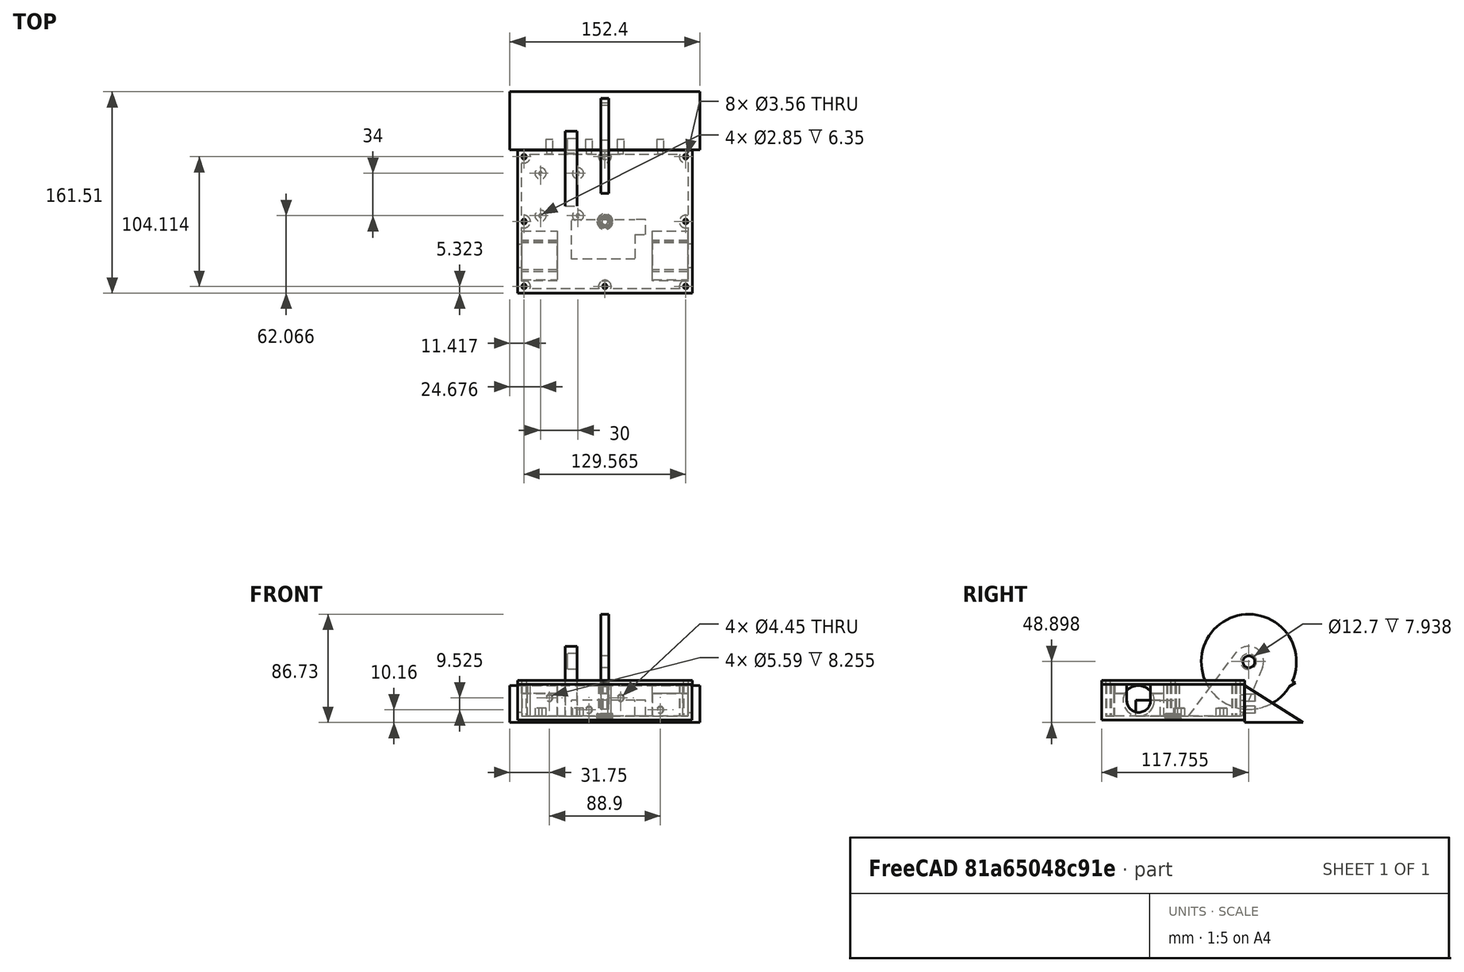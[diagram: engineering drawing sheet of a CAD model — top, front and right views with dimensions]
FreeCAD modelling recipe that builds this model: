
FCSTD DOCUMENT  (FreeCAD 0.20R)
Label: Isaac_combat_robot
License: All rights reserved
LicenseURL: http://en.wikipedia.org/wiki/All_rights_reserved
objects: Sketcher::SketchObject×22, PartDesign::Pad×14, PartDesign::Pocket×7, PartDesign::Body×7, Mesh::Feature×2, Spreadsheet::Sheet×1, PartDesign::ShapeBinder×1, PartDesign::Plane×1, PartDesign::FeatureBase×1, App::DocumentObjectGroup×1, Part::Feature×1
note: 75 computed .brp shape members not serialized (recipe doc carries the construction recipe); baked Part::Feature solids carry a one-line shape summary decoded from their .brp

FEATURE [Sketcher::SketchObject] Sketch
  FullyConstrained = true
  MapMode = 5
  Support = -> [XY_Plane]
  expr: Constraints[20] = Spreadsheet.wall_thickness
  expr: Constraints[21] = Spreadsheet.wall_thickness
  sketch-geometry (8):
    g0: LineSegment StartX=-69.85 StartY=57.15 StartZ=0 EndX=69.85 EndY=57.15 EndZ=0
    g1: LineSegment StartX=69.85 StartY=57.15 StartZ=0 EndX=69.85 EndY=-57.15 EndZ=0
    g2: LineSegment StartX=69.85 StartY=-57.15 StartZ=0 EndX=-69.85 EndY=-57.15 EndZ=0
    g3: LineSegment StartX=-69.85 StartY=-57.15 StartZ=0 EndX=-69.85 EndY=57.15 EndZ=0
    g4: LineSegment StartX=-66.675 StartY=53.975 StartZ=0 EndX=66.675 EndY=53.975 EndZ=0
    g5: LineSegment StartX=66.675 StartY=53.975 StartZ=0 EndX=66.675 EndY=-53.975 EndZ=0
    g6: LineSegment StartX=66.675 StartY=-53.975 StartZ=0 EndX=-66.675 EndY=-53.975 EndZ=0
    g7: LineSegment StartX=-66.675 StartY=-53.975 StartZ=0 EndX=-66.675 EndY=53.975 EndZ=0
  constraints (22):
    c: Coincident(g0,g1)
    c: Coincident(g1,g2)
    c: Coincident(g2,g3)
    c: Coincident(g3,g0)
    c: Horizontal(g0)
    c: Horizontal(g2)
    c: Vertical(g1)
    c: Vertical(g3)
    c: Symmetric(g1,g0,g-1)
    c: DistanceX(g0,g0) = 139.7
    c: DistanceY(g1,g1) = 114.3
    c: Coincident(g4,g5)
    c: Coincident(g5,g6)
    c: Coincident(g6,g7)
    c: Coincident(g7,g4)
    c: Horizontal(g4)
    c: Horizontal(g6)
    c: Vertical(g5)
    c: Vertical(g7)
    c: Symmetric(g5,g4,g-1)
    c: DistanceX(g4,g0) = 3.175
    c: DistanceY(g1,g5) = 3.175
FEATURE [Spreadsheet::Sheet] Spreadsheet
  cells = A1=wall thickness; B1(wall_thickness)==0.125 * 25.4; A2=height; B2(height)==1 * 25.4; A3=base_thickness; B3(base_thickness)==0.125 * 25.4
FEATURE [PartDesign::Pad] Pad  label="walls"
  Direction = (0,0,1)
  Length = 25.4
  Length2 = 100.013
  Profile = -> Sketch
  Type = 0
  expr: Length = Spreadsheet.height
FEATURE [Sketcher::SketchObject] Sketch001
  ExternalGeometry = -> [Pad]
  FullyConstrained = true
  MapMode = 5
  Placement = pos=(0,0,0) rot=(1,0,0;3.14159rad)
  Support = -> [Pad]
  sketch-geometry (4):
    g0: LineSegment StartX=69.85 StartY=57.15 StartZ=0 EndX=-69.85 EndY=57.15 EndZ=0
    g1: LineSegment StartX=-69.85 StartY=57.15 StartZ=0 EndX=-69.85 EndY=-57.15 EndZ=0
    g2: LineSegment StartX=-69.85 StartY=-57.15 StartZ=0 EndX=69.85 EndY=-57.15 EndZ=0
    g3: LineSegment StartX=69.85 StartY=-57.15 StartZ=0 EndX=69.85 EndY=57.15 EndZ=0
  constraints (10):
    c: Coincident(g0,g1)
    c: Coincident(g1,g2)
    c: Coincident(g2,g3)
    c: Coincident(g3,g0)
    c: Horizontal(g0)
    c: Horizontal(g2)
    c: Vertical(g1)
    c: Vertical(g3)
    c: Coincident(g0,g-3)
    c: Coincident(g1,g-4)
FEATURE [PartDesign::Pad] Pad001  label="base"
  BaseFeature = -> Pad
  Direction = (0,0,-1)
  Length = 3.175
  Length2 = 100.013
  Profile = -> Sketch001
  Type = 0
  expr: Length = Spreadsheet.base_thickness
FEATURE [Sketcher::SketchObject] Sketch002
  ExternalGeometry = -> [Pad001]
  FullyConstrained = true
  MapMode = 5
  Support = -> [Pad001]
  sketch-geometry (24):
    g0: LineSegment StartX=-64.77 StartY=52.07 StartZ=0 EndX=64.77 EndY=52.07 EndZ=0
    g1: LineSegment StartX=64.77 StartY=52.07 StartZ=0 EndX=64.77 EndY=-52.07 EndZ=0
    g2: LineSegment StartX=64.77 StartY=-52.07 StartZ=0 EndX=-64.77 EndY=-52.07 EndZ=0
    g3: LineSegment StartX=-64.77 StartY=-52.07 StartZ=0 EndX=-64.77 EndY=52.07 EndZ=0
    g4: GeomPoint X=-64.77 Y=0 Z=0
    g5: GeomPoint X=0 Y=52.07 Z=0
    g6: GeomPoint X=0 Y=-52.07 Z=0
    g7: GeomPoint X=64.77 Y=0 Z=0
    g8: Circle CenterX=-64.77 CenterY=52.07 CenterZ=0 NormalX=0 NormalY=0 NormalZ=1 AngleXU=0 Radius=5.08
    g9: Circle CenterX=0 CenterY=52.07 CenterZ=0 NormalX=0 NormalY=0 NormalZ=1 AngleXU=0 Radius=5.08
    g10: Circle CenterX=64.77 CenterY=52.07 CenterZ=0 NormalX=0 NormalY=0 NormalZ=1 AngleXU=0 Radius=5.08
    g11: Circle CenterX=64.77 CenterY=0 CenterZ=0 NormalX=0 NormalY=0 NormalZ=1 AngleXU=0 Radius=5.08
    g12: Circle CenterX=64.77 CenterY=-52.07 CenterZ=0 NormalX=0 NormalY=0 NormalZ=1 AngleXU=0 Radius=5.08
    g13: Circle CenterX=0 CenterY=-52.07 CenterZ=0 NormalX=0 NormalY=0 NormalZ=1 AngleXU=0 Radius=5.08
    g14: Circle CenterX=-64.77 CenterY=-52.07 CenterZ=0 NormalX=0 NormalY=0 NormalZ=1 AngleXU=0 Radius=5.08
    g15: Circle CenterX=-64.77 CenterY=0 CenterZ=0 NormalX=0 NormalY=0 NormalZ=1 AngleXU=0 Radius=5.08
    g16: Circle CenterX=-64.77 CenterY=52.07 CenterZ=0 NormalX=0 NormalY=0 NormalZ=1 AngleXU=0 Radius=2.413
    g17: Circle CenterX=0 CenterY=52.07 CenterZ=0 NormalX=0 NormalY=0 NormalZ=1 AngleXU=0 Radius=2.413
    g18: Circle CenterX=64.77 CenterY=52.07 CenterZ=0 NormalX=0 NormalY=0 NormalZ=1 AngleXU=0 Radius=2.413
    g19: Circle CenterX=64.77 CenterY=0 CenterZ=0 NormalX=0 NormalY=0 NormalZ=1 AngleXU=0 Radius=2.413
    g20: Circle CenterX=-64.77 CenterY=0 CenterZ=0 NormalX=0 NormalY=0 NormalZ=1 AngleXU=0 Radius=2.413
    g21: Circle CenterX=-64.77 CenterY=-52.07 CenterZ=0 NormalX=0 NormalY=0 NormalZ=1 AngleXU=0 Radius=2.413
    g22: Circle CenterX=0 CenterY=-52.07 CenterZ=0 NormalX=0 NormalY=0 NormalZ=1 AngleXU=0 Radius=2.413
    g23: Circle CenterX=64.77 CenterY=-52.07 CenterZ=0 NormalX=0 NormalY=0 NormalZ=1 AngleXU=0 Radius=2.413
  constraints (51):
    c: Coincident(g0,g1)
    c: Coincident(g1,g2)
    c: Coincident(g2,g3)
    c: Coincident(g3,g0)
    c: Horizontal(g0)
    c: Horizontal(g2)
    c: Vertical(g1)
    c: Vertical(g3)
    c: Symmetric(g1,g0,g-1)
    c: PointOnObject(g4,g3)
    c: PointOnObject(g5,g0)
    c: PointOnObject(g6,g2)
    c: PointOnObject(g7,g1)
    c: PointOnObject(g4,g-1)
    c: PointOnObject(g5,g-2)
    c: PointOnObject(g7,g-1)
    c: PointOnObject(g6,g-2)
    c: Coincident(g8,g0)
    c: Coincident(g9,g5)
    c: Coincident(g10,g0)
    c: Coincident(g11,g7)
    c: Coincident(g12,g1)
    c: Coincident(g13,g6)
    c: Coincident(g14,g2)
    c: Coincident(g15,g4)
    c: Equal(g14,g13)
    c: Equal(g13,g12)
    c: Equal(g12,g11)
    c: Equal(g11,g10)
    c: Equal(g10,g9)
    c: Equal(g9,g8)
    c: Equal(g8,g15)
    c: Diameter(g8) = 10.16
    c: Coincident(g16,g8)
    c: Coincident(g17,g9)
    c: Coincident(g18,g10)
    c: Coincident(g19,g11)
    c: Coincident(g20,g15)
    c: Coincident(g21,g14)
    c: Coincident(g22,g13)
    c: Coincident(g23,g12)
    c: Equal(g23,g22)
    c: Equal(g22,g21)
    c: Equal(g21,g20)
    c: Equal(g20,g16)
    c: Equal(g16,g17)
    c: Equal(g17,g18)
    c: Equal(g18,g19)
    c: Diameter(g18) = 4.826
    c: Tangent(g10,g-4)
    c: Tangent(g10,g-3)
FEATURE [PartDesign::Pad] Pad002  label="brass_insert_holes"
  BaseFeature = -> Pad001
  Direction = (0,0,1)
  Length = 25.4
  Length2 = 100.013
  Profile = -> Sketch002
  Type = 0
  expr: Length = Spreadsheet.height
FEATURE [Sketcher::SketchObject] Sketch003
  ExternalGeometry = -> [Pad002]
  FullyConstrained = true
  MapMode = 5
  Support = -> [Pad002]
  sketch-geometry (8):
    g0: LineSegment StartX=-69.85 StartY=-7.62 StartZ=0 EndX=-38.1 EndY=-7.62 EndZ=0
    g1: LineSegment StartX=-38.1 StartY=-7.62 StartZ=0 EndX=-38.1 EndY=-47.62 EndZ=0
    g2: LineSegment StartX=-38.1 StartY=-47.62 StartZ=0 EndX=-69.85 EndY=-47.62 EndZ=0
    g3: LineSegment StartX=-69.85 StartY=-47.62 StartZ=0 EndX=-69.85 EndY=-7.62 EndZ=0
    g4: LineSegment StartX=38.1 StartY=-7.62 StartZ=0 EndX=69.85 EndY=-7.62 EndZ=0
    g5: LineSegment StartX=69.85 StartY=-7.62 StartZ=0 EndX=69.85 EndY=-47.62 EndZ=0
    g6: LineSegment StartX=69.85 StartY=-47.62 StartZ=0 EndX=38.1 EndY=-47.62 EndZ=0
    g7: LineSegment StartX=38.1 StartY=-47.62 StartZ=0 EndX=38.1 EndY=-7.62 EndZ=0
  constraints (23):
    c: Coincident(g0,g1)
    c: Coincident(g1,g2)
    c: Coincident(g2,g3)
    c: Coincident(g3,g0)
    c: Horizontal(g0)
    c: Horizontal(g2)
    c: Vertical(g1)
    c: Vertical(g3)
    c: PointOnObject(g0,g-3)
    c: Coincident(g4,g5)
    c: Coincident(g5,g6)
    c: Coincident(g6,g7)
    c: Coincident(g7,g4)
    c: Horizontal(g4)
    c: Horizontal(g6)
    c: Vertical(g5)
    c: Vertical(g7)
    c: Equal(g4,g0)
    c: Equal(g1,g7)
    c: Symmetric(g0,g4,g-2)
    c: DistanceX(g0,g0) = 31.75
    c: DistanceY(g7,g7) = 40
    c: DistanceY(g0,g-1) = 7.62
FEATURE [PartDesign::Pad] Pad003  label="motor_pad"
  BaseFeature = -> Pad002
  Direction = (0,0,1)
  Length = 24.5
  Length2 = 99.9998
  Profile = -> Sketch003
  Type = 0
  expr: Length = 24.5mm
FEATURE [Sketcher::SketchObject] Sketch004
  ExternalGeometry = -> [Pad003]
  FullyConstrained = false
  MapMode = 5
  Placement = pos=(-69.85,0,0) rot=(0.57735,-0.57735,-0.57735;2.0944rad)
  Support = -> [Pad003]
  sketch-geometry (5):
    g0: LineSegment StartX=27.62 StartY=36.8625 StartZ=0 EndX=27.62 EndY=-14.5238 EndZ=0
    g1: ArcOfCircle CenterX=27.62 CenterY=12.4993 CenterZ=0 NormalX=0 NormalY=0 NormalZ=1 AngleXU=0 Radius=12.4993 StartAngle=2.43725 EndAngle=6.98752
    g2: LineSegment StartX=18.095 StartY=20.593 StartZ=0 EndX=18.095 EndY=26.943 EndZ=0
    g3: LineSegment StartX=18.095 StartY=26.943 StartZ=0 EndX=37.145 EndY=26.943 EndZ=0
    g4: LineSegment StartX=37.145 StartY=26.943 StartZ=0 EndX=37.145 EndY=20.593 EndZ=0
  constraints (14):
    c: Symmetric(g-4,g-3,g0)
    c: PointOnObject(g1,g0)
    c: Diameter(g1) = 24.9987
    c: Tangent(g1,g-1)
    c: Vertical(g2)
    c: Coincident(g3,g2)
    c: Coincident(g4,g3)
    c: Vertical(g4)
    c: Symmetric(g3,g2,g0)
    c: DistanceX(g3,g3) = 19.05
    c: Coincident(g1,g2)
    c: Coincident(g1,g4)
    c: DistanceY(g4,g4) = 6.35
    c: DistanceX(g-1,g0) = 27.62
FEATURE [PartDesign::Pocket] Pocket  label="drive_motor_pocket"
  BaseFeature = -> Pad003
  Direction = (1,0,0)
  Length = 5.0038
  Length2 = 99.9998
  Profile = -> Sketch004
  Type = 1
FEATURE [Sketcher::SketchObject] Sketch005  label="battery"
  FullyConstrained = false
  sketch-geometry (7):
    g0: LineSegment StartX=-55.3377 StartY=49.4576 StartZ=0 EndX=-23.5877 EndY=49.4576 EndZ=0
    g1: LineSegment StartX=-23.5877 StartY=49.4576 StartZ=0 EndX=-23.5877 EndY=-1.34242 EndZ=0
    g2: LineSegment StartX=-35.7299 StartY=-1.34242 StartZ=0 EndX=-55.3377 EndY=-1.34242 EndZ=0
    g3: LineSegment StartX=-55.3377 StartY=-1.34242 StartZ=0 EndX=-55.3377 EndY=49.4576 EndZ=0
    g4: LineSegment StartX=-35.7299 StartY=-1.34242 StartZ=0 EndX=-35.7299 EndY=-9.80609 EndZ=0
    g5: LineSegment StartX=-35.7299 StartY=-9.80609 StartZ=0 EndX=-23.5877 EndY=-9.80609 EndZ=0
    g6: LineSegment StartX=-23.5877 StartY=-9.80609 StartZ=0 EndX=-23.5877 EndY=-1.34242 EndZ=0
  constraints (14):
    c: Coincident(g0,g1)
    c: Coincident(g2,g3)
    c: Coincident(g3,g0)
    c: Horizontal(g0)
    c: Horizontal(g2)
    c: Vertical(g1)
    c: Vertical(g3)
    c: DistanceX(g0,g0) = 31.75
    c: DistanceY(g1,g1) = 50.8
    c: Coincident(g4,g5)
    c: Coincident(g5,g6)
    c: Horizontal(g5)
    c: Vertical(g4)
    c: Vertical(g6)
FEATURE [Sketcher::SketchObject] Sketch007  label="receiver_footprint"
  AttachmentOffset = pos=(-34.29,25.4,0) rot=(0,0,1;0rad)
  FullyConstrained = false
  MapMode = 5
  Placement = pos=(-34.29,25.4,0) rot=(0,0,1;0rad)
  sketch-geometry (12):
    g0: LineSegment StartX=-17.2344 StartY=13.2858 StartZ=0 EndX=12.7656 EndY=13.2858 EndZ=0
    g1: LineSegment StartX=12.7656 StartY=13.2858 StartZ=0 EndX=12.7656 EndY=-20.7142 EndZ=0
    g2: LineSegment StartX=12.7656 StartY=-20.7142 StartZ=0 EndX=-17.2344 EndY=-20.7142 EndZ=0
    g3: LineSegment StartX=-17.2344 StartY=-20.7142 StartZ=0 EndX=-17.2344 EndY=13.2858 EndZ=0
    g4: Circle CenterX=-17.2344 CenterY=13.2858 CenterZ=0 NormalX=0 NormalY=0 NormalZ=1 AngleXU=0 Radius=1.425
    g5: Circle CenterX=12.7656 CenterY=13.2858 CenterZ=0 NormalX=0 NormalY=0 NormalZ=1 AngleXU=0 Radius=1.425
    g6: Circle CenterX=12.7656 CenterY=-20.7142 CenterZ=0 NormalX=0 NormalY=0 NormalZ=1 AngleXU=0 Radius=1.425
    g7: Circle CenterX=-17.2344 CenterY=-20.7142 CenterZ=0 NormalX=0 NormalY=0 NormalZ=1 AngleXU=0 Radius=1.425
    g8: Circle CenterX=12.7656 CenterY=13.2858 CenterZ=0 NormalX=0 NormalY=0 NormalZ=1 AngleXU=0 Radius=4.445
    g9: Circle CenterX=-17.2344 CenterY=13.2858 CenterZ=0 NormalX=0 NormalY=0 NormalZ=1 AngleXU=0 Radius=4.445
    g10: Circle CenterX=-17.2344 CenterY=-20.7142 CenterZ=0 NormalX=0 NormalY=0 NormalZ=1 AngleXU=0 Radius=4.445
    g11: Circle CenterX=12.7656 CenterY=-20.7142 CenterZ=0 NormalX=0 NormalY=0 NormalZ=1 AngleXU=0 Radius=4.445
  constraints (26):
    c: Coincident(g0,g1)
    c: Coincident(g1,g2)
    c: Coincident(g2,g3)
    c: Coincident(g3,g0)
    c: Horizontal(g0)
    c: Horizontal(g2)
    c: Vertical(g1)
    c: Vertical(g3)
    c: Coincident(g4,g0)
    c: Coincident(g5,g0)
    c: Coincident(g6,g1)
    c: Coincident(g7,g2)
    c: Equal(g7,g6)
    c: Equal(g6,g5)
    c: Equal(g5,g4)
    c: Diameter(g5) = 2.85
    c: DistanceX(g0,g0) = 30
    c: DistanceY(g1,g1) = 34
    c: Coincident(g8,g5)
    c: Coincident(g9,g4)
    c: Coincident(g10,g7)
    c: Coincident(g11,g6)
    c: Equal(g10,g11)
    c: Equal(g11,g8)
    c: Equal(g8,g9)
    c: Diameter(g9) = 8.89
FEATURE [PartDesign::Pad] Pad006  label="receiver-pads"
  BaseFeature = -> Pocket
  Direction = (0,0,1)
  Length = 6.35
  Length2 = 99.9998
  Profile = -> Sketch007
  Type = 0
FEATURE [PartDesign::Pad] Pad007
  Direction = (1,1,1)
  Length = 12.7
  Length2 = 99.9998
  Profile = -> Sketch005
  Type = 0
FEATURE [PartDesign::Body] Body002  label="battery001"
  Group = -> [Sketch005,Pad007]
  Origin = -> Origin002
  Placement = pos=(22.86,25.4,0) rot=(0,0,1;1.5708rad)
  Tip = -> Pad007
FEATURE [PartDesign::ShapeBinder] ReferencePad006
  Support = -> [Pad006]
  TraceSupport = false
FEATURE [Sketcher::SketchObject] Sketch009  label="cover_plate"
  FullyConstrained = false
  MapMode = 5
  Placement = pos=(0,0,25.4) rot=(0,0,1;0rad)
  Support = -> [ReferencePad006]
  sketch-geometry (4):
    g0: LineSegment StartX=-70.0059 StartY=57.1862 StartZ=0 EndX=70.0536 EndY=57.1862 EndZ=0
    g1: LineSegment StartX=70.0536 StartY=57.1862 StartZ=0 EndX=70.0536 EndY=-57.385 EndZ=0
    g2: LineSegment StartX=70.0536 StartY=-57.385 StartZ=0 EndX=-70.0059 EndY=-57.385 EndZ=0
    g3: LineSegment StartX=-70.0059 StartY=-57.385 StartZ=0 EndX=-70.0059 EndY=57.1862 EndZ=0
  constraints (8):
    c: Coincident(g0,g1)
    c: Coincident(g1,g2)
    c: Coincident(g2,g3)
    c: Coincident(g3,g0)
    c: Horizontal(g0)
    c: Horizontal(g2)
    c: Vertical(g1)
    c: Vertical(g3)
FEATURE [PartDesign::Pad] Pad008
  Direction = (0,0,1)
  Length = 3.175
  Length2 = 99.9998
  Profile = -> Sketch009
  Type = 0
FEATURE [Mesh::Feature] body_half  label="switch_body_half"
  Placement = pos=(31.985,-47.375,0) rot=(1,0,0;1.5708rad)
FEATURE [Mesh::Feature] body_half001  label="switch_body_half001"
  Placement = pos=(44.985,-54.375,0) rot=(0,0.707107,0.707107;3.14159rad)
FEATURE [Sketcher::SketchObject] Sketch011
  FullyConstrained = false
  MapMode = 5
  Placement = pos=(0,0,0) rot=(0.57735,0.57735,0.57735;2.0944rad)
  Support = -> [YZ_Plane004]
  sketch-geometry (3):
    g0: LineSegment StartX=57.4696 StartY=-5.08 StartZ=0 EndX=104.128 EndY=-5.08 EndZ=0
    g1: LineSegment StartX=104.128 StartY=-5.08 StartZ=0 EndX=57.4696 EndY=24.511 EndZ=0
    g2: LineSegment StartX=57.4696 StartY=24.511 StartZ=0 EndX=57.4696 EndY=-5.08 EndZ=0
  constraints (7):
    c: Coincident(g0,g1)
    c: Coincident(g1,g2)
    c: Coincident(g2,g0)
    c: Vertical(g2)
    c: Horizontal(g0)
    c: DistanceY(g2,g2) = 29.591
    c: DistanceY(g0,g-1) = 5.08
FEATURE [PartDesign::Pad] Pad009  label="wedge-shape"
  Direction = (1,1,1)
  Length = 152.4
  Length2 = 99.9998
  Midplane = true
  Placement = pos=(0,0,0) rot=(0.57735,0.57735,0.57735;2.0944rad)
  Profile = -> Sketch011
  Type = 0
FEATURE [Sketcher::SketchObject] Sketch013  label="cover-holes"
  FullyConstrained = false
  MapMode = 5
  Placement = pos=(0,0,28.575) rot=(0,0,1;0rad)
  Support = -> [Pad008]
  sketch-geometry (16):
    g0: LineSegment StartX=-70.1798 StartY=57.1112 StartZ=0 EndX=70.1798 EndY=57.1112 EndZ=0
    g1: LineSegment StartX=70.1798 StartY=57.1112 StartZ=0 EndX=70.1798 EndY=-57.1112 EndZ=0
    g2: LineSegment StartX=70.1798 StartY=-57.1112 StartZ=0 EndX=-70.1798 EndY=-57.1112 EndZ=0
    g3: LineSegment StartX=-70.1798 StartY=-57.1112 StartZ=0 EndX=-70.1798 EndY=57.1112 EndZ=0
    g4: Circle CenterX=64.7827 CenterY=52.0568 CenterZ=0 NormalX=0 NormalY=0 NormalZ=1 AngleXU=0 Radius=1.778
    g5: Circle CenterX=64.7827 CenterY=0 CenterZ=0 NormalX=0 NormalY=0 NormalZ=1 AngleXU=0 Radius=1.778
    g6: Circle CenterX=64.7827 CenterY=-52.0568 CenterZ=0 NormalX=0 NormalY=0 NormalZ=1 AngleXU=0 Radius=1.778
    g7: LineSegment StartX=64.7827 StartY=52.0568 StartZ=0 EndX=-64.7827 EndY=52.0568 EndZ=0
    g8: LineSegment StartX=-64.7827 StartY=52.0568 StartZ=0 EndX=-64.7827 EndY=-52.0568 EndZ=0
    g9: LineSegment StartX=-64.7827 StartY=-52.0568 StartZ=0 EndX=64.7827 EndY=-52.0568 EndZ=0
    g10: LineSegment StartX=64.7827 StartY=-52.0568 StartZ=0 EndX=64.7827 EndY=52.0568 EndZ=0
    g11: Circle CenterX=0 CenterY=52.0568 CenterZ=0 NormalX=0 NormalY=0 NormalZ=1 AngleXU=0 Radius=1.778
    g12: Circle CenterX=-64.7827 CenterY=52.0568 CenterZ=0 NormalX=0 NormalY=0 NormalZ=1 AngleXU=0 Radius=1.778
    g13: Circle CenterX=-64.7827 CenterY=0.043989 CenterZ=0 NormalX=0 NormalY=0 NormalZ=1 AngleXU=0 Radius=1.778
    g14: Circle CenterX=-64.7827 CenterY=-52.0568 CenterZ=0 NormalX=0 NormalY=0 NormalZ=1 AngleXU=0 Radius=1.778
    g15: Circle CenterX=0 CenterY=-52.0568 CenterZ=0 NormalX=0 NormalY=0 NormalZ=1 AngleXU=0 Radius=1.778
  constraints (37):
    c: Coincident(g0,g1)
    c: Coincident(g1,g2)
    c: Coincident(g2,g3)
    c: Coincident(g3,g0)
    c: Horizontal(g0)
    c: Horizontal(g2)
    c: Vertical(g1)
    c: Vertical(g3)
    c: Symmetric(g1,g0,g-1)
    c: PointOnObject(g5,g-1)
    c: Coincident(g7,g8)
    c: Coincident(g8,g9)
    c: Coincident(g9,g10)
    c: Coincident(g10,g7)
    c: Horizontal(g7)
    c: Horizontal(g9)
    c: Vertical(g8)
    c: Vertical(g10)
    c: Coincident(g7,g4)
    c: PointOnObject(g11,g7)
    c: Coincident(g12,g7)
    c: PointOnObject(g13,g8)
    c: Coincident(g14,g8)
    c: PointOnObject(g15,g9)
    c: PointOnObject(g15,g-2)
    c: Equal(g4,g11)
    c: Equal(g11,g12)
    c: Equal(g12,g13)
    c: Equal(g13,g14)
    c: Equal(g14,g15)
    c: Equal(g15,g6)
    c: Equal(g6,g5)
    c: Radius(g4) = 1.778
    c: Symmetric(g14,g4,g-1)
    c: PointOnObject(g11,g-2)
    c: PointOnObject(g5,g10)
    c: Coincident(g6,g9)
FEATURE [PartDesign::Pocket] Pocket003
  BaseFeature = -> Pad008
  Direction = (0,0,-1)
  Length = 5.00126
  Length2 = 99.9998
  Profile = -> Sketch013
  Type = 0
FEATURE [Sketcher::SketchObject] Sketch014  label="wedge_mount_holes"
  FullyConstrained = false
  MapMode = 5
  Placement = pos=(0,53.975,0) rot=(1,0,0;1.5708rad)
  Support = -> [Pad006]
  sketch-geometry (6):
    g0: Circle CenterX=-44.45 CenterY=14.605 CenterZ=0 NormalX=0 NormalY=0 NormalZ=1 AngleXU=0 Radius=2.2225
    g1: Circle CenterX=-12.7 CenterY=5.08 CenterZ=0 NormalX=0 NormalY=0 NormalZ=1 AngleXU=0 Radius=2.2225
    g2: Circle CenterX=12.7 CenterY=14.605 CenterZ=0 NormalX=0 NormalY=0 NormalZ=1 AngleXU=0 Radius=2.2225
    g3: Circle CenterX=44.45 CenterY=5.08 CenterZ=0 NormalX=0 NormalY=0 NormalZ=1 AngleXU=0 Radius=2.2225
    g4: LineSegment StartX=-12.7 StartY=48.9484 StartZ=0 EndX=-12.7 EndY=-7.89198 EndZ=0
    g5: LineSegment StartX=12.7 StartY=48.9484 StartZ=0 EndX=12.7 EndY=2.06139 EndZ=0
  constraints (15):
    c: DistanceY(g1,g0) = 9.525
    c: DistanceX(g0,g1) = 31.75
    c: Horizontal(g2,g0)
    c: Horizontal(g3,g1)
    c: Vertical(g4)
    c: Vertical(g5)
    c: DistanceX(g4,g-1) = 12.7
    c: PointOnObject(g1,g4)
    c: Symmetric(g4,g5,g-2)
    c: PointOnObject(g2,g5)
    c: DistanceY(g-1,g1) = 5.08
    c: Equal(g0,g1)
    c: Equal(g1,g2)
    c: Equal(g2,g3)
    c: Diameter(g0) = 4.445
FEATURE [PartDesign::Pocket] Pocket004  label="wedge-mount-holes"
  BaseFeature = -> Pad006
  Direction = (0,1,-2e-16)
  Length = 5
  Length2 = 5
  Profile = -> Sketch014
  ReferenceAxis = -> Sketch014 [N_Axis]
  Type = 1
FEATURE [Sketcher::SketchObject] Sketch015
  FullyConstrained = false
  MapMode = 5
  Placement = pos=(0,0,24.5) rot=(0,0,1;0rad)
  Support = -> [Pocket004]
  sketch-geometry (6):
    g0: LineSegment StartX=-66.675 StartY=-6.35 StartZ=0 EndX=66.675 EndY=-6.35 EndZ=0
    g1: LineSegment StartX=66.675 StartY=-6.35 StartZ=0 EndX=66.675 EndY=-47.752 EndZ=0
    g2: LineSegment StartX=66.675 StartY=-47.752 StartZ=0 EndX=-66.675 EndY=-47.752 EndZ=0
    g3: LineSegment StartX=-66.675 StartY=-47.752 StartZ=0 EndX=-66.675 EndY=-6.35 EndZ=0
    g4: LineSegment StartX=-83.3972 StartY=-6.35 StartZ=0 EndX=91.5592 EndY=-6.35 EndZ=0
    g5: LineSegment StartX=0 StartY=16.9837 StartZ=0 EndX=0 EndY=-68.8496 EndZ=0
  constraints (15):
    c: Coincident(g0,g1)
    c: Coincident(g1,g2)
    c: Coincident(g2,g3)
    c: Coincident(g3,g0)
    c: Horizontal(g0)
    c: Horizontal(g2)
    c: Vertical(g1)
    c: Vertical(g3)
    c: DistanceX(g0,g0) = 133.35
    c: DistanceY(g3,g3) = 41.402
    c: Horizontal(g4)
    c: DistanceY(g4,g-1) = 6.35
    c: PointOnObject(g4,g0)
    c: PointOnObject(g5,g-2)
    c: Symmetric(g0,g0,g5)
FEATURE [PartDesign::Pocket] Pocket005  label="motor-mount-subtraction"
  BaseFeature = -> Pocket004
  Direction = (0,0,-1)
  Length = 6.35
  Length2 = 5
  Profile = -> Sketch015
  ReferenceAxis = -> Sketch015 [N_Axis]
  Type = 0
FEATURE [Sketcher::SketchObject] Sketch016  label="motor-retainer"
  ExternalGeometry = -> [Pocket005]
  FullyConstrained = true
  MapMode = 5
  Placement = pos=(-69.85,0,0) rot=(0.57735,-0.57735,-0.57735;2.0944rad)
  Support = -> [Pocket005]
  sketch-geometry (4):
    g0: ArcOfCircle CenterX=27.62 CenterY=12.4993 CenterZ=0 NormalX=0 NormalY=0 NormalZ=1 AngleXU=0 Radius=9.525 StartAngle=3.14159 EndAngle=6.28319
    g1: ArcOfCircle CenterX=27.62 CenterY=12.4993 CenterZ=0 NormalX=0 NormalY=0 NormalZ=1 AngleXU=0 Radius=12.7 StartAngle=2.41886 EndAngle=7.00592
    g2: LineSegment StartX=18.095 StartY=20.8996 StartZ=0 EndX=18.095 EndY=12.4994 EndZ=0
    g3: LineSegment StartX=37.145 StartY=20.8996 StartZ=0 EndX=37.145 EndY=12.4994 EndZ=0
  constraints (12):
    c: Diameter(g0) = 19.05
    c: Diameter(g1) = 25.4
    c: Coincident(g0,g3)
    c: Coincident(g0,g2)
    c: Coincident(g1,g3)
    c: Coincident(g1,g2)
    c: Vertical(g3)
    c: Horizontal(g0,g0)
    c: Horizontal(g1,g1)
    c: DistanceX(g0,g0) = 19.05
    c: Coincident(g0,g1)
    c: Coincident(g0,g-4)
FEATURE [PartDesign::Pad] Pad010  label="motor-retainer-R"
  BaseFeature = -> Pocket005
  Direction = (-1,0,0)
  Length = 3.175
  Length2 = 10
  Profile = -> Sketch016
  ReferenceAxis = -> Sketch016 [N_Axis]
  Reversed = true
  Type = 0
FEATURE [Sketcher::SketchObject] Sketch018  label="wedge_mount_holes001"
  AttachmentOffset = pos=(0,0,0) rot=(0,0,1;1.5708rad)
  FullyConstrained = false
  MapMode = 5
  Placement = pos=(2.5e-14,57.4696,-1.3e-14) rot=(1,0,0;1.5708rad)
  sketch-geometry (6):
    g0: Circle CenterX=-44.45 CenterY=14.605 CenterZ=0 NormalX=0 NormalY=0 NormalZ=1 AngleXU=0 Radius=2.794
    g1: Circle CenterX=-12.7 CenterY=5.08 CenterZ=0 NormalX=0 NormalY=0 NormalZ=1 AngleXU=0 Radius=2.794
    g2: Circle CenterX=12.7 CenterY=14.605 CenterZ=0 NormalX=0 NormalY=0 NormalZ=1 AngleXU=0 Radius=2.794
    g3: Circle CenterX=44.45 CenterY=5.08 CenterZ=0 NormalX=0 NormalY=0 NormalZ=1 AngleXU=0 Radius=2.794
    g4: LineSegment StartX=-12.7 StartY=48.9484 StartZ=0 EndX=-12.7 EndY=-7.89198 EndZ=0
    g5: LineSegment StartX=12.7 StartY=48.9484 StartZ=0 EndX=12.7 EndY=2.06139 EndZ=0
  constraints (15):
    c: DistanceY(g1,g0) = 9.525
    c: DistanceX(g0,g1) = 31.75
    c: Horizontal(g2,g0)
    c: Horizontal(g3,g1)
    c: Vertical(g4)
    c: Vertical(g5)
    c: DistanceX(g4,g-1) = 12.7
    c: PointOnObject(g1,g4)
    c: Symmetric(g4,g5,g-2)
    c: PointOnObject(g2,g5)
    c: DistanceY(g-1,g1) = 5.08
    c: Equal(g0,g1)
    c: Equal(g1,g2)
    c: Equal(g2,g3)
    c: Diameter(g0) = 5.588
FEATURE [Sketcher::SketchObject] Sketch019  label="motor-retainer001"
  ExternalGeometry = -> [Pocket005]
  FullyConstrained = true
  MapMode = 5
  Placement = pos=(69.85,0,0) rot=(0.57735,0.57735,0.57735;2.0944rad)
  Support = -> [Pocket005]
  sketch-geometry (4):
    g0: ArcOfCircle CenterX=-27.62 CenterY=12.4993 CenterZ=0 NormalX=0 NormalY=0 NormalZ=1 AngleXU=0 Radius=12.7 StartAngle=2.41886 EndAngle=7.00592
    g1: ArcOfCircle CenterX=-27.62 CenterY=12.4993 CenterZ=0 NormalX=0 NormalY=0 NormalZ=1 AngleXU=0 Radius=9.525 StartAngle=3.1416 EndAngle=6.28319
    g2: LineSegment StartX=-37.145 StartY=20.8996 StartZ=0 EndX=-37.145 EndY=12.4993 EndZ=0
    g3: LineSegment StartX=-18.095 StartY=20.8996 StartZ=0 EndX=-18.095 EndY=12.4993 EndZ=0
  constraints (12):
    c: Coincident(g0,g-4)
    c: Coincident(g1,g0)
    c: Diameter(g1) = 19.05
    c: Diameter(g0) = 25.4
    c: Vertical(g3)
    c: Vertical(g2)
    c: Coincident(g1,g3)
    c: Coincident(g1,g2)
    c: Coincident(g0,g3)
    c: Coincident(g0,g2)
    c: Vertical(g0,g-4)
    c: Vertical(g0,g-3)
FEATURE [PartDesign::Pad] Pad011  label="motor-retainer-L"
  BaseFeature = -> Pad010
  Direction = (1,0,0)
  Length = 3.175
  Length2 = 10
  Profile = -> Sketch019
  ReferenceAxis = -> Sketch019 [N_Axis]
  Reversed = true
  Type = 0
FEATURE [PartDesign::Body] Body  label="main_body"
  Group = -> [Sketch,Pad,Sketch001,Pad001,Sketch002,Pad002,Sketch003,Pad003,Sketch004,Pocket,Sketch007,Pad006,Sketch014,Pocket004,Sketch015,Pocket005,Sketch016,Pad010,Sketch019,Pad011]
  Origin = -> Origin
  Tip = -> Pad011
FEATURE [PartDesign::Pocket] Pocket006  label="screw-holes"
  BaseFeature = -> Pad009
  Direction = (2e-16,1,-2e-16)
  Length = 8.255
  Length2 = 5
  Placement = pos=(0,0,0) rot=(0.57735,0.57735,0.57735;2.0944rad)
  Profile = -> Sketch018
  ReferenceAxis = -> Sketch018 [N_Axis]
  Type = 0
FEATURE [PartDesign::Body] Body004  label="wedge"
  Group = -> [Sketch011,Pad009,Sketch018,Pocket006]
  Origin = -> Origin004
  Tip = -> Pocket006
FEATURE [Sketcher::SketchObject] Sketch020
  FullyConstrained = true
  MapMode = 5
  Placement = pos=(0,0,25.4) rot=(1,0,0;3.14159rad)
  Support = -> [Pad008]
  sketch-geometry (4):
    g0: LineSegment StartX=-66.675 StartY=46.736 StartZ=0 EndX=66.675 EndY=46.736 EndZ=0
    g1: LineSegment StartX=66.675 StartY=46.736 StartZ=0 EndX=66.675 EndY=7.62 EndZ=0
    g2: LineSegment StartX=66.675 StartY=7.62 StartZ=0 EndX=-66.675 EndY=7.62 EndZ=0
    g3: LineSegment StartX=-66.675 StartY=7.62 StartZ=0 EndX=-66.675 EndY=46.736 EndZ=0
  constraints (11):
    c: Coincident(g0,g1)
    c: Coincident(g1,g2)
    c: Coincident(g2,g3)
    c: Coincident(g3,g0)
    c: Horizontal(g2)
    c: Vertical(g1)
    c: Vertical(g3)
    c: Symmetric(g0,g0,g-2)
    c: DistanceY(g1,g1) = 39.116
    c: DistanceY(g-1,g1) = 7.62
    c: DistanceX(g0,g0) = 133.35
FEATURE [PartDesign::Pad] Pad012  label="motor-top-pad"
  BaseFeature = -> Pocket003
  Direction = (0,0,-1)
  Length = 6.985
  Length2 = 10
  Profile = -> Sketch020
  ReferenceAxis = -> Sketch020 [N_Axis]
  Type = 0
FEATURE [Sketcher::SketchObject] Sketch021  label="motor-pocket"
  FullyConstrained = false
  MapMode = 5
  Placement = pos=(-66.675,0,0) rot=(0.57735,-0.57735,-0.57735;2.0944rad)
  Support = -> [Pad012]
  sketch-geometry (2):
    g0: Circle CenterX=27.94 CenterY=11.9913 CenterZ=0 NormalX=0 NormalY=0 NormalZ=1 AngleXU=0 Radius=12.4993
    g1: LineSegment StartX=-10.2857 StartY=-0.508 StartZ=0 EndX=65.7759 EndY=-0.508 EndZ=0
  constraints (5):
    c: Diameter(g0) = 24.9987
    c: Horizontal(g1)
    c: DistanceY(g1,g-1) = 0.508
    c: Tangent(g0,g1)
    c: DistanceX(g-1,g0) = 27.94
FEATURE [PartDesign::Pocket] Pocket007  label="motor-pocket001"
  BaseFeature = -> Pad012
  Direction = (1,0,0)
  Length = 5
  Length2 = 5
  Profile = -> Sketch021
  ReferenceAxis = -> Sketch021 [N_Axis]
  Type = 1
FEATURE [Sketcher::SketchObject] Sketch022
  FullyConstrained = true
  MapMode = 5
  Placement = pos=(0,0,25.4) rot=(1,0,0;3.14159rad)
  Support = -> [Pocket007]
  sketch-geometry (4):
    g0: LineSegment StartX=-38.1 StartY=49.53 StartZ=0 EndX=38.1 EndY=49.53 EndZ=0
    g1: LineSegment StartX=38.1 StartY=49.53 StartZ=0 EndX=38.1 EndY=6.35 EndZ=0
    g2: LineSegment StartX=38.1 StartY=6.35 StartZ=0 EndX=-38.1 EndY=6.35 EndZ=0
    g3: LineSegment StartX=-38.1 StartY=6.35 StartZ=0 EndX=-38.1 EndY=49.53 EndZ=0
  constraints (11):
    c: Coincident(g0,g1)
    c: Coincident(g1,g2)
    c: Coincident(g2,g3)
    c: Coincident(g3,g0)
    c: Horizontal(g2)
    c: Vertical(g1)
    c: Vertical(g3)
    c: Symmetric(g0,g0,g-2)
    c: DistanceY(g-1,g1) = 6.35
    c: DistanceY(g1,g1) = 43.18
    c: DistanceX(g0,g0) = 76.2
FEATURE [PartDesign::Pocket] Pocket008  label="center-removal"
  BaseFeature = -> Pocket007
  Direction = (0,0,1)
  Length = 8.89
  Length2 = 5
  Profile = -> Sketch022
  ReferenceAxis = -> Sketch022 [N_Axis]
  Reversed = true
  Type = 0
FEATURE [PartDesign::Body] Body003  label="top_cover"
  Group = -> [ReferencePad006,Sketch009,Pad008,Sketch013,Pocket003,Sketch020,Pad012,Sketch021,Pocket007,Sketch022,Pocket008]
  Origin = -> Origin003
  Tip = -> Pocket008
FEATURE [Sketcher::SketchObject] Sketch023
  FullyConstrained = false
  MapMode = 5
  Support = -> [Pad010]
  sketch-geometry (8):
    g0: LineSegment StartX=19.05 StartY=52.6099 StartZ=0 EndX=28.575 EndY=52.6099 EndZ=0
    g1: LineSegment StartX=28.575 StartY=52.6099 StartZ=0 EndX=28.575 EndY=14.5099 EndZ=0
    g2: LineSegment StartX=28.575 StartY=14.5099 StartZ=0 EndX=19.05 EndY=14.5099 EndZ=0
    g3: LineSegment StartX=19.05 StartY=14.5099 StartZ=0 EndX=19.05 EndY=52.6099 EndZ=0
    g4: LineSegment StartX=-28.575 StartY=52.6099 StartZ=0 EndX=-19.05 EndY=52.6099 EndZ=0
    g5: LineSegment StartX=-19.05 StartY=52.6099 StartZ=0 EndX=-19.05 EndY=14.5099 EndZ=0
    g6: LineSegment StartX=-19.05 StartY=14.5099 StartZ=0 EndX=-28.575 EndY=14.5099 EndZ=0
    g7: LineSegment StartX=-28.575 StartY=14.5099 StartZ=0 EndX=-28.575 EndY=52.6099 EndZ=0
  constraints (22):
    c: Coincident(g0,g1)
    c: Coincident(g1,g2)
    c: Coincident(g2,g3)
    c: Coincident(g3,g0)
    c: Horizontal(g0)
    c: Horizontal(g2)
    c: Vertical(g1)
    c: Vertical(g3)
    c: Coincident(g4,g5)
    c: Coincident(g5,g6)
    c: Coincident(g6,g7)
    c: Coincident(g7,g4)
    c: Horizontal(g4)
    c: Horizontal(g6)
    c: Vertical(g5)
    c: Vertical(g7)
    c: Symmetric(g5,g2,g-2)
    c: Equal(g6,g2)
    c: DistanceX(g5,g2) = 38.1
    c: Equal(g5,g3)
    c: DistanceY(g1,g1) = 38.1
    c: DistanceX(g0,g0) = 9.525
FEATURE [Sketcher::SketchObject] Sketch024
  AttachmentOffset = pos=(0,0,19.05) rot=(0,0,1;0rad)
  FullyConstrained = false
  MapMode = 5
  Placement = pos=(19.05,-4.2e-15,4.2e-15) rot=(0.57735,0.57735,0.57735;2.0944rad)
  Support = -> [YZ_Plane005]
  sketch-geometry (6):
    g0: LineSegment StartX=12.3806 StartY=0 StartZ=0 EndX=50.6577 EndY=51.0974 EndZ=0
    g1: LineSegment StartX=71.5702 StartY=39.1184 StartZ=0 EndX=55.1483 EndY=0 EndZ=0
    g2: LineSegment StartX=55.1483 StartY=0 StartZ=0 EndX=12.3806 EndY=0 EndZ=0
    g3: Circle CenterX=60.3751 CenterY=43.8181 CenterZ=0 NormalX=0 NormalY=0 NormalZ=1 AngleXU=0 Radius=38.1
    g4: ArcOfCircle CenterX=60.3751 CenterY=43.8181 CenterZ=0 NormalX=0 NormalY=0 NormalZ=1 AngleXU=0 Radius=12.1415 StartAngle=5.88573 EndAngle=8.78185
    g5: Circle CenterX=60.3751 CenterY=43.8181 CenterZ=0 NormalX=0 NormalY=0 NormalZ=1 AngleXU=0 Radius=6.35
  constraints (10):
    c: PointOnObject(g0,g-1)
    c: PointOnObject(g1,g-1)
    c: Coincident(g1,g2)
    c: Coincident(g2,g0)
    c: Diameter(g3) = 76.2
    c: Coincident(g3,g4)
    c: Tangent(g4,g1) = 1.5708
    c: Tangent(g4,g0) = 1.5708
    c: Coincident(g5,g4)
    c: Diameter(g5) = 12.7
FEATURE [PartDesign::Plane] DatumPlane
  Length = 115.238
  MapMode = 49
  Placement = pos=(0,0,0) rot=(0.57735,0.57735,0.57735;2.0944rad)
  ResizeMode = 0
  Width = 98.7168
FEATURE [PartDesign::Pad] Pad013  label="weapon_mount"
  Direction = (1,-2e-16,3e-16)
  Length = 9.525
  Length2 = 10
  Placement = pos=(0,0,0) rot=(0.57735,0.57735,0.57735;2.0944rad)
  Profile = -> Sketch024
  ReferenceAxis = -> Sketch024 [N_Axis]
  Type = 0
FEATURE [Sketcher::SketchObject] Sketch025
  FullyConstrained = false
  MapMode = 5
  Placement = pos=(19.05,-7.6e-15,6e-15) rot=(0.57735,0.57735,-0.57735;4.18879rad)
  Support = -> [Pad013]
  sketch-geometry (2):
    g0: Circle CenterX=60.4685 CenterY=-43.8035 CenterZ=0 NormalX=0 NormalY=0 NormalZ=1 AngleXU=0 Radius=7.85664
    g1: Circle CenterX=60.4685 CenterY=-43.8035 CenterZ=0 NormalX=0 NormalY=0 NormalZ=1 AngleXU=0 Radius=5.0366
  constraints (1):
    c: Coincident(g1,g0)
FEATURE [PartDesign::Pad] Pad014  label="bearing_retainer"
  BaseFeature = -> Pad013
  Direction = (-1,7e-16,-3e-16)
  Length = 1.5875
  Length2 = 10
  Placement = pos=(0,0,0) rot=(0.57735,0.57735,0.57735;2.0944rad)
  Profile = -> Sketch025
  ReferenceAxis = -> Sketch025 [N_Axis]
  Reversed = true
  Type = 0
FEATURE [PartDesign::Body] Body005  label="wmount"
  Group = -> [Sketch023,Sketch024,DatumPlane,Pad013,Sketch025,Pad014]
  Origin = -> Origin005
  Tip = -> Pad014
FEATURE [PartDesign::FeatureBase] Clone
  BaseFeature = -> Body005
FEATURE [PartDesign::Body] Body006  label="wmountl"
  Group = -> [Clone]
  Origin = -> Origin006
  Placement = pos=(-50.8,0,0) rot=(0,0,1;0rad)
  Tip = -> Clone
FEATURE [App::DocumentObjectGroup] Group  label="weapon"
  Group = -> [Body005,Body006]
FEATURE [Sketcher::SketchObject] Sketch026
  FullyConstrained = false
  MapMode = 5
  Placement = pos=(0,0,0) rot=(0.57735,0.57735,0.57735;2.0944rad)
  Support = -> [YZ_Plane007]
  sketch-geometry (4):
    g0: ArcOfCircle CenterX=60.6216 CenterY=43.5453 CenterZ=0 NormalX=0 NormalY=0 NormalZ=1 AngleXU=0 Radius=38.1 StartAngle=5.86244 EndAngle=12.028
    g1: Circle CenterX=60.6216 CenterY=43.5453 CenterZ=0 NormalX=0 NormalY=0 NormalZ=1 AngleXU=0 Radius=4.7625
    g2: LineSegment StartX=93.333 StartY=24.0113 StartZ=0 EndX=98.0821 EndY=26.8383 EndZ=0
    g3: LineSegment StartX=98.0821 StartY=26.8383 StartZ=0 EndX=95.3987 EndY=27.9837 EndZ=0
  constraints (6):
    c: Diameter(g0) = 76.2
    c: Coincident(g1,g0)
    c: Diameter(g1) = 9.525
    c: Coincident(g3,g2)
    c: Coincident(g0,g2)
    c: Coincident(g0,g3)
FEATURE [PartDesign::Pad] Pad015
  Direction = (1,-2e-16,3e-16)
  Length = 6.35
  Length2 = 10
  Midplane = true
  Placement = pos=(0,0,0) rot=(0.57735,0.57735,0.57735;2.0944rad)
  Profile = -> Sketch026
  ReferenceAxis = -> Sketch026 [N_Axis]
  Type = 0
FEATURE [PartDesign::Body] Body007
  Group = -> [Sketch026,Pad015]
  Origin = -> Origin007
  Tip = -> Pad015
FEATURE [Part::Feature] Part__Feature  label="60355K132_Ball Bearing"
  shape: bbox 13.75 x 13.75 x 3.97 mm, 528 faces, 18 solids (baked)
